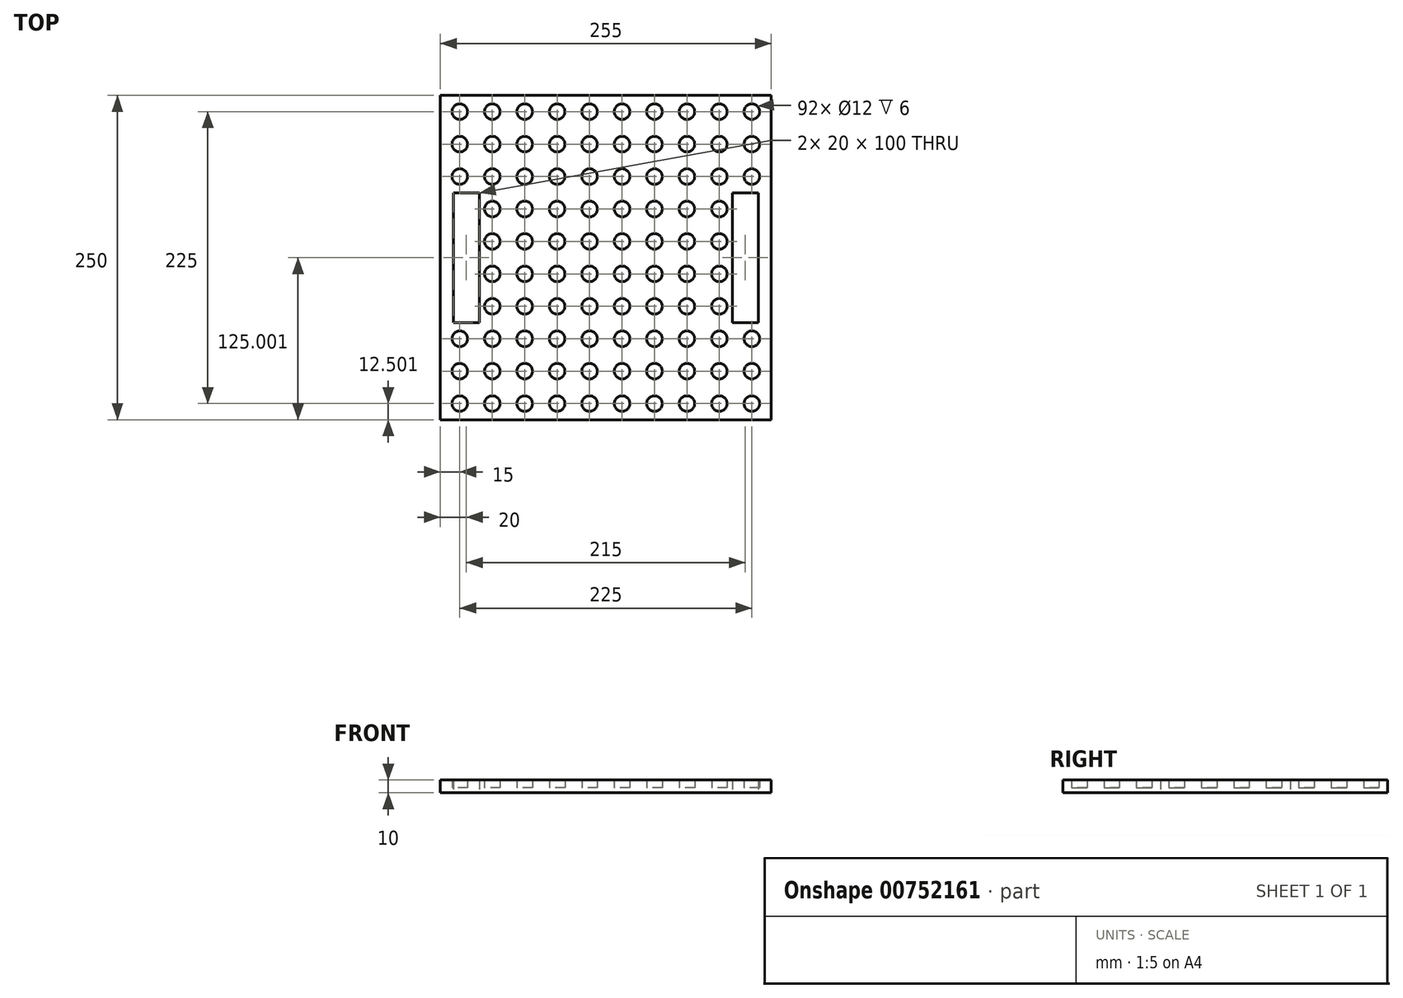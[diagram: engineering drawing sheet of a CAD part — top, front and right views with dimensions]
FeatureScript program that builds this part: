
annotation { "Feature Type Name" : "Feature", "Feature Type Description" : "" }
export const myFeature = defineFeature(function(context is Context, id is Id, definition is map)
    precondition{}
    {
        {
            var Q0;
            Q0=qCreatedBy(makeId("Top.planeOp"),FACE);
            var sketch = newSketch(context, id + "F0", { "sketchPlane" : qUnion([Q0])});
            skLineSegment(sketch, "E0.bottom", {"start": v(127.5, -329.86) * mm, "end": v(-127.5, -329.86) * mm});
            skLineSegment(sketch, "E0.top", {"start": v(127.5, -79.86) * mm, "end": v(-127.5, -79.86) * mm});
            skLineSegment(sketch, "E0.left", {"start": v(127.5, -329.86) * mm, "end": v(127.5, -79.86) * mm});
            skLineSegment(sketch, "E0.right", {"start": v(-127.5, -329.86) * mm, "end": v(-127.5, -79.86) * mm});
            skLineSegment(sketch, "E1.bottom", {"start": v(117.5, -254.86) * mm, "end": v(97.5, -254.86) * mm});
            skLineSegment(sketch, "E1.top", {"start": v(117.5, -154.86) * mm, "end": v(97.5, -154.86) * mm});
            skLineSegment(sketch, "E1.left", {"start": v(117.5, -254.86) * mm, "end": v(117.5, -154.86) * mm});
            skLineSegment(sketch, "E1.right", {"start": v(97.5, -254.86) * mm, "end": v(97.5, -154.86) * mm});
            skLineSegment(sketch, "E2.MirrorCS", {"start": v(-117.5, -154.86) * mm, "end": v(-97.5, -154.86) * mm});
            skLineSegment(sketch, "E3.MirrorCS", {"start": v(-97.5, -254.86) * mm, "end": v(-97.5, -154.86) * mm});
            skLineSegment(sketch, "E4.MirrorCS", {"start": v(-117.5, -254.86) * mm, "end": v(-97.5, -254.86) * mm});
            skLineSegment(sketch, "E5.MirrorCS", {"start": v(-117.5, -254.86) * mm, "end": v(-117.5, -154.86) * mm});
            skCircle(sketch, "E6", {"center": v(-112.5, -92.36) * mm, "radius": 6 * mm});
            skCircle(sketch, "E7.1.0.0", {"center": v(-87.5, -92.36) * mm, "radius": 6 * mm});
            skCircle(sketch, "E7.2.0.0", {"center": v(-62.5, -92.36) * mm, "radius": 6 * mm});
            skCircle(sketch, "E8.0.3.0", {"center": v(-37.5, -92.36) * mm, "radius": 6 * mm});
            skCircle(sketch, "E8.0.4.0", {"center": v(-12.5, -92.36) * mm, "radius": 6 * mm});
            skCircle(sketch, "E8.0.5.0", {"center": v(12.5, -92.36) * mm, "radius": 6 * mm});
            skCircle(sketch, "E8.0.6.0", {"center": v(37.5, -92.36) * mm, "radius": 6 * mm});
            skCircle(sketch, "E8.0.7.0", {"center": v(62.5, -92.36) * mm, "radius": 6 * mm});
            skCircle(sketch, "E8.0.8.0", {"center": v(87.5, -92.36) * mm, "radius": 6 * mm});
            skCircle(sketch, "E8.0.9.0", {"center": v(112.5, -92.36) * mm, "radius": 6 * mm});
            skCircle(sketch, "E9.0.1.0", {"center": v(-112.5, -117.36) * mm, "radius": 6 * mm});
            skCircle(sketch, "E9.0.1.1", {"center": v(-37.5, -117.36) * mm, "radius": 6 * mm});
            skCircle(sketch, "E9.0.1.2", {"center": v(12.5, -117.36) * mm, "radius": 6 * mm});
            skCircle(sketch, "E9.0.2.0", {"center": v(-112.5, -142.36) * mm, "radius": 6 * mm});
            skCircle(sketch, "E9.0.2.1", {"center": v(-37.5, -142.36) * mm, "radius": 6 * mm});
            skCircle(sketch, "E9.0.2.2", {"center": v(12.5, -142.36) * mm, "radius": 6 * mm});
            skCircle(sketch, "E9.0.3.1", {"center": v(-37.5, -167.36) * mm, "radius": 6 * mm});
            skCircle(sketch, "E9.0.3.2", {"center": v(12.5, -167.36) * mm, "radius": 6 * mm});
            skCircle(sketch, "E9.0.4.1", {"center": v(-37.5, -192.36) * mm, "radius": 6 * mm});
            skCircle(sketch, "E9.0.4.2", {"center": v(12.5, -192.36) * mm, "radius": 6 * mm});
            skCircle(sketch, "E9.0.5.1", {"center": v(-37.5, -217.36) * mm, "radius": 6 * mm});
            skCircle(sketch, "E9.0.5.2", {"center": v(12.5, -217.36) * mm, "radius": 6 * mm});
            skCircle(sketch, "E9.0.6.1", {"center": v(-37.5, -242.36) * mm, "radius": 6 * mm});
            skCircle(sketch, "E9.0.6.2", {"center": v(12.5, -242.36) * mm, "radius": 6 * mm});
            skCircle(sketch, "E9.0.7.0", {"center": v(-112.5, -267.36) * mm, "radius": 6 * mm});
            skCircle(sketch, "E9.0.7.1", {"center": v(-37.5, -267.36) * mm, "radius": 6 * mm});
            skCircle(sketch, "E9.0.7.2", {"center": v(12.5, -267.36) * mm, "radius": 6 * mm});
            skCircle(sketch, "E9.0.8.0", {"center": v(-112.5, -292.36) * mm, "radius": 6 * mm});
            skCircle(sketch, "E9.0.8.1", {"center": v(-37.5, -292.36) * mm, "radius": 6 * mm});
            skCircle(sketch, "E9.0.8.2", {"center": v(12.5, -292.36) * mm, "radius": 6 * mm});
            skCircle(sketch, "E9.0.9.0", {"center": v(-112.5, -317.36) * mm, "radius": 6 * mm});
            skCircle(sketch, "E9.0.9.1", {"center": v(-37.5, -317.36) * mm, "radius": 6 * mm});
            skCircle(sketch, "E9.0.9.2", {"center": v(12.5, -317.36) * mm, "radius": 6 * mm});
            skCircle(sketch, "E9.1.1.0", {"center": v(-87.5, -117.36) * mm, "radius": 6 * mm});
            skCircle(sketch, "E9.1.1.1", {"center": v(-12.5, -117.36) * mm, "radius": 6 * mm});
            skCircle(sketch, "E9.1.1.2", {"center": v(37.5, -117.36) * mm, "radius": 6 * mm});
            skCircle(sketch, "E9.1.2.0", {"center": v(-87.5, -142.36) * mm, "radius": 6 * mm});
            skCircle(sketch, "E9.1.2.1", {"center": v(-12.5, -142.36) * mm, "radius": 6 * mm});
            skCircle(sketch, "E9.1.2.2", {"center": v(37.5, -142.36) * mm, "radius": 6 * mm});
            skCircle(sketch, "E9.1.3.0", {"center": v(-87.5, -167.36) * mm, "radius": 6 * mm});
            skCircle(sketch, "E9.1.3.1", {"center": v(-12.5, -167.36) * mm, "radius": 6 * mm});
            skCircle(sketch, "E9.1.3.2", {"center": v(37.5, -167.36) * mm, "radius": 6 * mm});
            skCircle(sketch, "E9.1.4.0", {"center": v(-87.5, -192.36) * mm, "radius": 6 * mm});
            skCircle(sketch, "E9.1.4.1", {"center": v(-12.5, -192.36) * mm, "radius": 6 * mm});
            skCircle(sketch, "E9.1.4.2", {"center": v(37.5, -192.36) * mm, "radius": 6 * mm});
            skCircle(sketch, "E9.1.5.0", {"center": v(-87.5, -217.36) * mm, "radius": 6 * mm});
            skCircle(sketch, "E9.1.5.1", {"center": v(-12.5, -217.36) * mm, "radius": 6 * mm});
            skCircle(sketch, "E9.1.5.2", {"center": v(37.5, -217.36) * mm, "radius": 6 * mm});
            skCircle(sketch, "E9.1.6.0", {"center": v(-87.5, -242.36) * mm, "radius": 6 * mm});
            skCircle(sketch, "E9.1.6.1", {"center": v(-12.5, -242.36) * mm, "radius": 6 * mm});
            skCircle(sketch, "E9.1.6.2", {"center": v(37.5, -242.36) * mm, "radius": 6 * mm});
            skCircle(sketch, "E9.1.7.0", {"center": v(-87.5, -267.36) * mm, "radius": 6 * mm});
            skCircle(sketch, "E9.1.7.1", {"center": v(-12.5, -267.36) * mm, "radius": 6 * mm});
            skCircle(sketch, "E9.1.7.2", {"center": v(37.5, -267.36) * mm, "radius": 6 * mm});
            skCircle(sketch, "E9.1.8.0", {"center": v(-87.5, -292.36) * mm, "radius": 6 * mm});
            skCircle(sketch, "E9.1.8.1", {"center": v(-12.5, -292.36) * mm, "radius": 6 * mm});
            skCircle(sketch, "E9.1.8.2", {"center": v(37.5, -292.36) * mm, "radius": 6 * mm});
            skCircle(sketch, "E9.1.9.0", {"center": v(-87.5, -317.36) * mm, "radius": 6 * mm});
            skCircle(sketch, "E9.1.9.1", {"center": v(-12.5, -317.36) * mm, "radius": 6 * mm});
            skCircle(sketch, "E9.1.9.2", {"center": v(37.5, -317.36) * mm, "radius": 6 * mm});
            skCircle(sketch, "E9.2.1.0", {"center": v(-62.5, -117.36) * mm, "radius": 6 * mm});
            skCircle(sketch, "E9.2.1.1", {"center": v(12.5, -117.36) * mm, "radius": 6 * mm});
            skCircle(sketch, "E9.2.1.2", {"center": v(62.5, -117.36) * mm, "radius": 6 * mm});
            skCircle(sketch, "E9.2.2.0", {"center": v(-62.5, -142.36) * mm, "radius": 6 * mm});
            skCircle(sketch, "E9.2.2.1", {"center": v(12.5, -142.36) * mm, "radius": 6 * mm});
            skCircle(sketch, "E9.2.2.2", {"center": v(62.5, -142.36) * mm, "radius": 6 * mm});
            skCircle(sketch, "E9.2.3.0", {"center": v(-62.5, -167.36) * mm, "radius": 6 * mm});
            skCircle(sketch, "E9.2.3.1", {"center": v(12.5, -167.36) * mm, "radius": 6 * mm});
            skCircle(sketch, "E9.2.3.2", {"center": v(62.5, -167.36) * mm, "radius": 6 * mm});
            skCircle(sketch, "E9.2.4.0", {"center": v(-62.5, -192.36) * mm, "radius": 6 * mm});
            skCircle(sketch, "E9.2.4.1", {"center": v(12.5, -192.36) * mm, "radius": 6 * mm});
            skCircle(sketch, "E9.2.4.2", {"center": v(62.5, -192.36) * mm, "radius": 6 * mm});
            skCircle(sketch, "E9.2.5.0", {"center": v(-62.5, -217.36) * mm, "radius": 6 * mm});
            skCircle(sketch, "E9.2.5.1", {"center": v(12.5, -217.36) * mm, "radius": 6 * mm});
            skCircle(sketch, "E9.2.5.2", {"center": v(62.5, -217.36) * mm, "radius": 6 * mm});
            skCircle(sketch, "E9.2.6.0", {"center": v(-62.5, -242.36) * mm, "radius": 6 * mm});
            skCircle(sketch, "E9.2.6.1", {"center": v(12.5, -242.36) * mm, "radius": 6 * mm});
            skCircle(sketch, "E9.2.6.2", {"center": v(62.5, -242.36) * mm, "radius": 6 * mm});
            skCircle(sketch, "E9.2.7.0", {"center": v(-62.5, -267.36) * mm, "radius": 6 * mm});
            skCircle(sketch, "E9.2.7.1", {"center": v(12.5, -267.36) * mm, "radius": 6 * mm});
            skCircle(sketch, "E9.2.7.2", {"center": v(62.5, -267.36) * mm, "radius": 6 * mm});
            skCircle(sketch, "E9.2.8.0", {"center": v(-62.5, -292.36) * mm, "radius": 6 * mm});
            skCircle(sketch, "E9.2.8.1", {"center": v(12.5, -292.36) * mm, "radius": 6 * mm});
            skCircle(sketch, "E9.2.8.2", {"center": v(62.5, -292.36) * mm, "radius": 6 * mm});
            skCircle(sketch, "E9.2.9.0", {"center": v(-62.5, -317.36) * mm, "radius": 6 * mm});
            skCircle(sketch, "E9.2.9.1", {"center": v(12.5, -317.36) * mm, "radius": 6 * mm});
            skCircle(sketch, "E9.2.9.2", {"center": v(62.5, -317.36) * mm, "radius": 6 * mm});
            skCircle(sketch, "E10.MirrorC", {"center": v(112.5, -117.36) * mm, "radius": 6 * mm});
            skCircle(sketch, "E11.MirrorC", {"center": v(112.5, -317.36) * mm, "radius": 6 * mm});
            skCircle(sketch, "E12.MirrorC", {"center": v(112.5, -142.36) * mm, "radius": 6 * mm});
            skCircle(sketch, "E13.MirrorC", {"center": v(112.5, -267.36) * mm, "radius": 6 * mm});
            skCircle(sketch, "E14.MirrorC", {"center": v(112.5, -292.36) * mm, "radius": 6 * mm});
            skCircle(sketch, "E15.MirrorC", {"center": v(87.5, -267.36) * mm, "radius": 6 * mm});
            skCircle(sketch, "E16.MirrorC", {"center": v(87.5, -317.36) * mm, "radius": 6 * mm});
            skCircle(sketch, "E17.MirrorC", {"center": v(87.5, -217.36) * mm, "radius": 6 * mm});
            skCircle(sketch, "E18.MirrorC", {"center": v(87.5, -117.36) * mm, "radius": 6 * mm});
            skCircle(sketch, "E19.MirrorC", {"center": v(87.5, -292.36) * mm, "radius": 6 * mm});
            skCircle(sketch, "E20.MirrorC", {"center": v(87.5, -167.36) * mm, "radius": 6 * mm});
            skCircle(sketch, "E21.MirrorC", {"center": v(87.5, -242.36) * mm, "radius": 6 * mm});
            skCircle(sketch, "E22.MirrorC", {"center": v(87.5, -142.36) * mm, "radius": 6 * mm});
            skCircle(sketch, "E23.MirrorC", {"center": v(87.5, -192.36) * mm, "radius": 6 * mm});
            skSolve(sketch);
        }
        {
            var Q0;
            Q0=makeQuery(id+"F0.imprint","IMPRINT",FACE,{"disambiguationData":[TD([[makeQuery(id+"F0.imprint","IMPRINT",EDGE,{"derivedFrom":sQuery(id+"F0.wireOp",EDGE,"E0.bottom")}),-1.0]])]});
            extrude(context, id + "F1", {"entities" : qUnion([Q0]), "depth" : 6 * mm, "offsetDistance" : 25 * mm});
        }
        {
            var Q0;
            Q0=makeQuery(id+"F1.opExtrude","CAP_FACE",FACE,{"disambiguationData":[OSD([sQuery(id+"F0.wireOp",EDGE,"E0.bottom"),sQuery(id+"F0.wireOp",EDGE,"E0.top"),sQuery(id+"F0.wireOp",EDGE,"E0.left"),sQuery(id+"F0.wireOp",EDGE,"E0.right"),sQuery(id+"F0.wireOp",EDGE,"E1.bottom"),sQuery(id+"F0.wireOp",EDGE,"E1.top"),sQuery(id+"F0.wireOp",EDGE,"E1.left"),sQuery(id+"F0.wireOp",EDGE,"E1.right"),sQuery(id+"F0.wireOp",EDGE,"E2.MirrorCS"),sQuery(id+"F0.wireOp",EDGE,"E3.MirrorCS"),sQuery(id+"F0.wireOp",EDGE,"E4.MirrorCS"),sQuery(id+"F0.wireOp",EDGE,"E5.MirrorCS"),sQuery(id+"F0.wireOp",EDGE,"E6"),sQuery(id+"F0.wireOp",EDGE,"E8.0.3.0"),sQuery(id+"F0.wireOp",EDGE,"E9.0.1.0"),sQuery(id+"F0.wireOp",EDGE,"E9.0.1.1"),sQuery(id+"F0.wireOp",EDGE,"E9.0.2.0"),sQuery(id+"F0.wireOp",EDGE,"E9.0.2.1"),sQuery(id+"F0.wireOp",EDGE,"E9.0.3.1"),sQuery(id+"F0.wireOp",EDGE,"E9.0.4.1"),sQuery(id+"F0.wireOp",EDGE,"E9.0.5.1"),sQuery(id+"F0.wireOp",EDGE,"E9.0.6.1"),sQuery(id+"F0.wireOp",EDGE,"E9.0.7.0"),sQuery(id+"F0.wireOp",EDGE,"E9.0.7.1"),sQuery(id+"F0.wireOp",EDGE,"E9.0.8.0"),sQuery(id+"F0.wireOp",EDGE,"E9.0.8.1"),sQuery(id+"F0.wireOp",EDGE,"E9.0.9.0"),sQuery(id+"F0.wireOp",EDGE,"E9.0.9.1"),sQuery(id+"F0.wireOp",EDGE,"E7.1.0.0"),sQuery(id+"F0.wireOp",EDGE,"E8.0.4.0"),sQuery(id+"F0.wireOp",EDGE,"E8.0.6.0"),sQuery(id+"F0.wireOp",EDGE,"E9.1.1.0"),sQuery(id+"F0.wireOp",EDGE,"E9.1.1.1"),sQuery(id+"F0.wireOp",EDGE,"E9.1.1.2"),sQuery(id+"F0.wireOp",EDGE,"E9.1.2.0"),sQuery(id+"F0.wireOp",EDGE,"E9.1.2.1"),sQuery(id+"F0.wireOp",EDGE,"E9.1.2.2"),sQuery(id+"F0.wireOp",EDGE,"E9.1.3.0"),sQuery(id+"F0.wireOp",EDGE,"E9.1.3.1"),sQuery(id+"F0.wireOp",EDGE,"E9.1.3.2"),sQuery(id+"F0.wireOp",EDGE,"E9.1.4.0"),sQuery(id+"F0.wireOp",EDGE,"E9.1.4.1"),sQuery(id+"F0.wireOp",EDGE,"E9.1.4.2"),sQuery(id+"F0.wireOp",EDGE,"E9.1.5.0"),sQuery(id+"F0.wireOp",EDGE,"E9.1.5.1"),sQuery(id+"F0.wireOp",EDGE,"E9.1.5.2"),sQuery(id+"F0.wireOp",EDGE,"E9.1.6.0"),sQuery(id+"F0.wireOp",EDGE,"E9.1.6.1"),sQuery(id+"F0.wireOp",EDGE,"E9.1.6.2"),sQuery(id+"F0.wireOp",EDGE,"E9.1.7.0"),sQuery(id+"F0.wireOp",EDGE,"E9.1.7.1"),sQuery(id+"F0.wireOp",EDGE,"E9.1.7.2"),sQuery(id+"F0.wireOp",EDGE,"E9.1.8.0"),sQuery(id+"F0.wireOp",EDGE,"E9.1.8.1"),sQuery(id+"F0.wireOp",EDGE,"E9.1.8.2"),sQuery(id+"F0.wireOp",EDGE,"E9.1.9.0"),sQuery(id+"F0.wireOp",EDGE,"E9.1.9.1"),sQuery(id+"F0.wireOp",EDGE,"E9.1.9.2"),sQuery(id+"F0.wireOp",EDGE,"E7.2.0.0"),sQuery(id+"F0.wireOp",EDGE,"E8.0.5.0"),sQuery(id+"F0.wireOp",EDGE,"E8.0.7.0"),sQuery(id+"F0.wireOp",EDGE,"E9.2.1.0"),sQuery(id+"F0.wireOp",EDGE,"E9.2.1.1"),sQuery(id+"F0.wireOp",EDGE,"E9.2.1.2"),sQuery(id+"F0.wireOp",EDGE,"E9.2.2.0"),sQuery(id+"F0.wireOp",EDGE,"E9.2.2.1"),sQuery(id+"F0.wireOp",EDGE,"E9.2.2.2"),sQuery(id+"F0.wireOp",EDGE,"E9.2.3.0"),sQuery(id+"F0.wireOp",EDGE,"E9.2.3.1"),sQuery(id+"F0.wireOp",EDGE,"E9.2.3.2"),sQuery(id+"F0.wireOp",EDGE,"E9.2.4.0"),sQuery(id+"F0.wireOp",EDGE,"E9.2.4.1"),sQuery(id+"F0.wireOp",EDGE,"E9.2.4.2"),sQuery(id+"F0.wireOp",EDGE,"E9.2.5.0"),sQuery(id+"F0.wireOp",EDGE,"E9.2.5.1"),sQuery(id+"F0.wireOp",EDGE,"E9.2.5.2"),sQuery(id+"F0.wireOp",EDGE,"E9.2.6.0"),sQuery(id+"F0.wireOp",EDGE,"E9.2.6.1"),sQuery(id+"F0.wireOp",EDGE,"E9.2.6.2"),sQuery(id+"F0.wireOp",EDGE,"E9.2.7.0"),sQuery(id+"F0.wireOp",EDGE,"E9.2.7.1"),sQuery(id+"F0.wireOp",EDGE,"E9.2.7.2"),sQuery(id+"F0.wireOp",EDGE,"E9.2.8.0"),sQuery(id+"F0.wireOp",EDGE,"E9.2.8.1"),sQuery(id+"F0.wireOp",EDGE,"E9.2.8.2"),sQuery(id+"F0.wireOp",EDGE,"E9.2.9.0"),sQuery(id+"F0.wireOp",EDGE,"E9.2.9.1"),sQuery(id+"F0.wireOp",EDGE,"E9.2.9.2"),sQuery(id+"F0.wireOp",EDGE,"E15.MirrorC"),sQuery(id+"F0.wireOp",EDGE,"E14.MirrorC"),sQuery(id+"F0.wireOp",EDGE,"E16.MirrorC"),sQuery(id+"F0.wireOp",EDGE,"E8.0.9.0"),sQuery(id+"F0.wireOp",EDGE,"E13.MirrorC"),sQuery(id+"F0.wireOp",EDGE,"E17.MirrorC"),sQuery(id+"F0.wireOp",EDGE,"E18.MirrorC"),sQuery(id+"F0.wireOp",EDGE,"E19.MirrorC"),sQuery(id+"F0.wireOp",EDGE,"E8.0.8.0"),sQuery(id+"F0.wireOp",EDGE,"E11.MirrorC"),sQuery(id+"F0.wireOp",EDGE,"E20.MirrorC"),sQuery(id+"F0.wireOp",EDGE,"E10.MirrorC"),sQuery(id+"F0.wireOp",EDGE,"E21.MirrorC"),sQuery(id+"F0.wireOp",EDGE,"E22.MirrorC"),sQuery(id+"F0.wireOp",EDGE,"E23.MirrorC"),sQuery(id+"F0.wireOp",EDGE,"E12.MirrorC")])],"isStart":true});
            var sketch = newSketch(context, id + "F2", { "sketchPlane" : qUnion([Q0])});
            skLineSegment(sketch, "E24.bottom", {"start": v(-127.5, 329.86) * mm, "end": v(127.5, 329.86) * mm});
            skLineSegment(sketch, "E24.top", {"start": v(-127.5, 79.86) * mm, "end": v(127.5, 79.86) * mm});
            skLineSegment(sketch, "E24.left", {"start": v(-127.5, 329.86) * mm, "end": v(-127.5, 79.86) * mm});
            skLineSegment(sketch, "E24.right", {"start": v(127.5, 329.86) * mm, "end": v(127.5, 79.86) * mm});
            skLineSegment(sketch, "E25.bottom", {"start": v(-117.5, 254.86) * mm, "end": v(-97.5, 254.86) * mm});
            skLineSegment(sketch, "E25.top", {"start": v(-117.5, 154.86) * mm, "end": v(-97.5, 154.86) * mm});
            skLineSegment(sketch, "E25.left", {"start": v(-117.5, 254.86) * mm, "end": v(-117.5, 154.86) * mm});
            skLineSegment(sketch, "E25.right", {"start": v(-97.5, 254.86) * mm, "end": v(-97.5, 154.86) * mm});
            skLineSegment(sketch, "E26.bottom", {"start": v(97.5, 254.86) * mm, "end": v(117.5, 254.86) * mm});
            skLineSegment(sketch, "E26.top", {"start": v(97.5, 154.86) * mm, "end": v(117.5, 154.86) * mm});
            skLineSegment(sketch, "E26.left", {"start": v(97.5, 254.86) * mm, "end": v(97.5, 154.86) * mm});
            skLineSegment(sketch, "E26.right", {"start": v(117.5, 254.86) * mm, "end": v(117.5, 154.86) * mm});
            skSolve(sketch);
        }
        {
            var Q0;
            Q0 = qSketchRegion(id + "F2", true);
            extrude(context, id + "F3", {"entities" : qUnion([Q0]), "operationType" : NewBodyOperationType.ADD, "depth" : 4 * mm, "offsetDistance" : 25 * mm});
        }
    });
